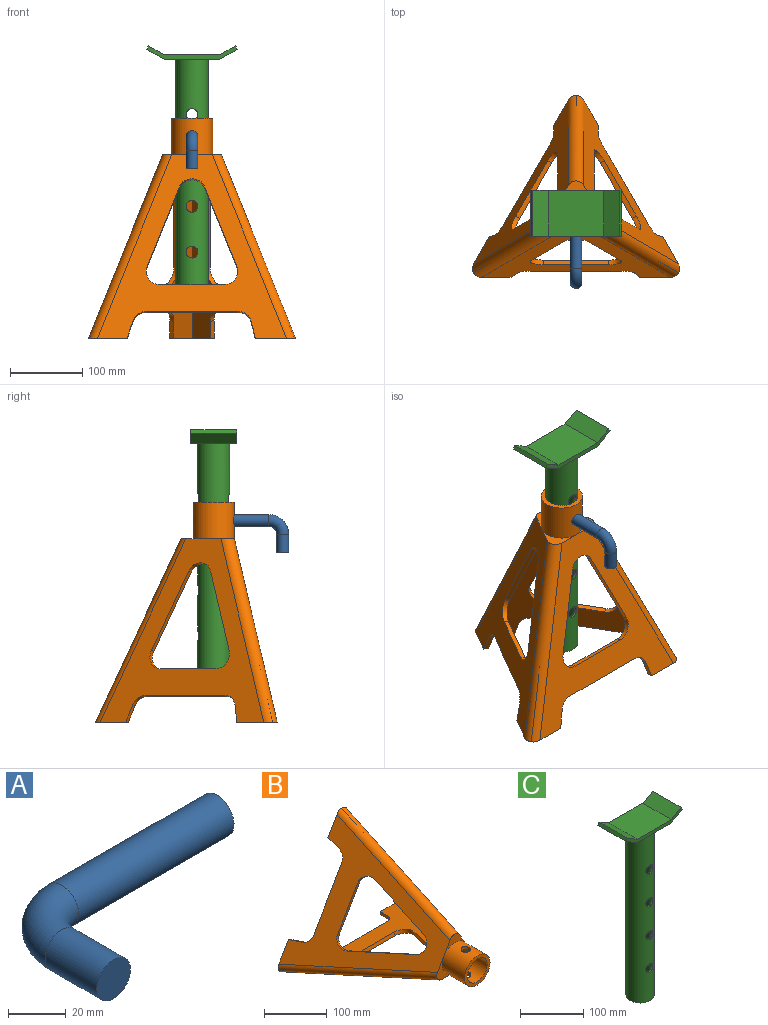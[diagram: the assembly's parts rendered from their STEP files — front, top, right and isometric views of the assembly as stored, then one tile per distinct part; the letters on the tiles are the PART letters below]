
ASSEMBLY  parts=3 mates=2
PART A: 5 faces, bbox 105.8x55x16.5 mm
  f0: plane 16.51x16.51mm, normal (0,-1,0), area 214.1mm2, adj f2
  f1: plane 16.51x16.51mm, normal (1,0,0), area 214.1mm2, adj f4
  f2: cylinder r=8.26mm len=25.4mm, axis (0,1,0), area 1317.4mm2, adj f0,f3
  f3: torus R=19.05mm, axis (0,0,-1), area 1552.1mm2, adj f2,f4
  f4: cylinder r=8.26mm len=76.2mm, axis (1,0,0), area 3952.3mm2, adj f1,f3
PART B: 56 faces, bbox 287.7x307.4x252.5 mm
  f0: plane 38.5x33.34mm, normal (0,1,0), area 338.3mm2, adj f4,f10,f15
  f1: plane 38.5x33.34mm, normal (0,1,0), area 338.3mm2, adj f7,f10,f15
  f2: plane 55.97x53.98mm, normal (0,1,0), area 638.6mm2, adj f3,f4,f6,f7,f20,f35,f45
  f3: plane 261.96x254mm, normal (0,-0.23,-0.97), area 22759.7mm2, adj f2,f8,f11,f13,f20,f21,f45,f46
  f4: plane 282.86x247.71mm, normal (0,0.23,0.97), area 27340.8mm2, adj f0,f2,f7,f8,f10,f14,f45,f46
  f5: plane 62.38x45.55mm, normal (0,1,0), area 624.7mm2, adj f6,f7,f9,f10,f22,f23,f34
  f6: plane 254x226.87mm, normal (-0.84,-0.23,0.49), area 22759.7mm2, adj f2,f5,f12,f13,f20,f22,f34,f35
  f7: plane 247.71x244.97mm, normal (0.84,0.23,-0.49), area 27340.8mm2, adj f1,f2,f4,f5,f10,f14,f34,f35
  f8: plane 56.09x55.97mm, normal (0,1,0), area 652.4mm2, adj f3,f4,f9,f10,f21,f27,f46
  f9: plane 254x226.87mm, normal (0.84,-0.23,0.49), area 22759.7mm2, adj f5,f8,f11,f12,f21,f22,f23,f24
  f10: plane 247.71x244.97mm, normal (-0.84,0.23,-0.49), area 27340.8mm2, adj f0,f1,f4,f5,f7,f8,f23,f24
  f11: plane 42.86x40.61mm, normal (0,-1,0), area 458.5mm2, adj f3,f9,f16,f21
  f12: plane 49.49x30.8mm, normal (0,-1,0), area 458.5mm2, adj f6,f9,f16,f22
  f13: plane 42.86x40.61mm, normal (0,-1,0), area 458.5mm2, adj f3,f6,f16,f20
  f14: plane 38.5x33.34mm, normal (0,1,0), area 338.3mm2, adj f4,f7,f15
  f15: cylinder r=22.23mm len=57.15mm, axis (0,1,0), area 7577.8mm2, adj f0,f1,f14,f17,f18,f19
  f16: cylinder r=28.57mm len=57.15mm, axis (0,1,0), area 8721mm2, adj f11,f12,f13,f17,f18,f19
  f17: plane 57.15x57.15mm, normal (0,-1,0), area 1013.4mm2, adj f15,f16
  f18: cylinder r=7.94mm len=15.88mm, axis (0,0,1), area 325mm2, adj f15,f16
  f19: cylinder r=7.94mm len=15.88mm, axis (0,0,1), area 325.1mm2, adj f15,f16
  f20: cylinder r=12.7mm len=258.99mm, axis (-0.37,0.91,-0.21), area 7146.4mm2, adj f2,f3,f6,f13
  f21: cylinder r=12.7mm len=258.99mm, axis (0.37,0.91,-0.21), area 7146.4mm2, adj f3,f8,f9,f11
  f22: cylinder r=12.7mm len=258.99mm, axis (0,0.91,0.42), area 7146.4mm2, adj f5,f6,f9,f12
  f23: plane 24.47x13.27mm, normal (0.54,0.31,-0.78), area 161mm2, adj f5,f9,f10,f24
  f24: cylinder r=19.05mm len=20.22mm, axis (0.84,-0.23,0.49), area 150.8mm2, adj f9,f10,f23,f25
  f25: plane 113.1x68.89mm, normal (0.2,0.97,0.11), area 811.7mm2, adj f9,f10,f24,f26
  f26: cylinder r=19.05mm len=17.51mm, axis (0.84,-0.23,0.49), area 161mm2, adj f9,f10,f25,f27
  f27: plane 22.96x12.86mm, normal (-0.44,0.23,0.87), area 146.9mm2, adj f8,f9,f10,f26
  f28: cylinder r=19.05mm len=34.33mm, axis (0.84,-0.23,0.49), area 338.7mm2, adj f9,f10,f29,f33
  f29: plane 111.25x50.69mm, normal (-0.39,0.36,0.85), area 857mm2, adj f9,f10,f28,f30
  f30: cylinder r=19.05mm len=26.9mm, axis (0.84,-0.23,0.49), area 247.8mm2, adj f9,f10,f29,f31
  f31: plane 80.21x50.02mm, normal (-0.2,-0.97,-0.11), area 587.4mm2, adj f9,f10,f30,f32
  f32: cylinder r=19.05mm len=26.9mm, axis (0.84,-0.23,0.49), area 247.8mm2, adj f9,f10,f31,f33
  f33: plane 111.25x54.93mm, normal (0.54,0.36,-0.76), area 857mm2, adj f9,f10,f28,f32
  f34: plane 24.47x13.27mm, normal (-0.54,0.31,-0.78), area 161mm2, adj f5,f6,f7,f38
  f35: plane 22.96x12.86mm, normal (0.44,0.23,0.87), area 146.9mm2, adj f2,f6,f7,f36
  f36: cylinder r=19.05mm len=17.51mm, axis (-0.84,-0.23,0.49), area 161mm2, adj f6,f7,f35,f37
  f37: plane 113.1x68.89mm, normal (-0.2,0.97,0.11), area 811.7mm2, adj f6,f7,f36,f38
  f38: cylinder r=19.05mm len=20.22mm, axis (-0.84,-0.23,0.49), area 150.8mm2, adj f6,f7,f34,f37
  f39: cylinder r=19.05mm len=34.33mm, axis (-0.84,-0.23,0.49), area 338.7mm2, adj f6,f7,f40,f44
  f40: plane 111.25x54.93mm, normal (-0.54,0.36,-0.76), area 857mm2, adj f6,f7,f39,f41
  f41: cylinder r=19.05mm len=26.9mm, axis (-0.84,-0.23,0.49), area 247.8mm2, adj f6,f7,f40,f42
  f42: plane 80.21x50.02mm, normal (0.2,-0.97,-0.11), area 587.4mm2, adj f6,f7,f41,f43
  f43: cylinder r=19.05mm len=26.9mm, axis (-0.84,-0.23,0.49), area 247.8mm2, adj f6,f7,f42,f44
  f44: plane 111.25x50.69mm, normal (0.39,0.36,0.85), area 857mm2, adj f6,f7,f39,f43
  f45: plane 24.47x11.88mm, normal (0.95,0.31,-0.07), area 161mm2, adj f2,f3,f4,f49
  f46: plane 22.96x11.51mm, normal (-0.97,0.23,-0.05), area 146.9mm2, adj f3,f4,f8,f47
  f47: cylinder r=19.05mm len=18.5mm, axis (0,-0.23,-0.97), area 161mm2, adj f3,f4,f46,f48
  f48: plane 127x6.22mm, normal (0,0.97,-0.23), area 811.7mm2, adj f3,f4,f47,f49
  f49: cylinder r=19.05mm len=18.05mm, axis (0,-0.23,-0.97), area 150.8mm2, adj f3,f4,f45,f48
  f50: cylinder r=19.05mm len=35.44mm, axis (0,-0.23,-0.97), area 338.7mm2, adj f3,f4,f51,f55
  f51: plane 111.25x44.45mm, normal (0.93,0.36,-0.08), area 857mm2, adj f3,f4,f50,f52
  f52: cylinder r=19.05mm len=26.9mm, axis (0,-0.23,-0.97), area 247.8mm2, adj f3,f4,f51,f53
  f53: plane 88.9x6.43mm, normal (0,-0.97,0.23), area 587.4mm2, adj f3,f4,f52,f54
  f54: cylinder r=19.05mm len=26.9mm, axis (0,-0.23,-0.97), area 247.8mm2, adj f3,f4,f53,f55
  f55: plane 111.25x44.45mm, normal (-0.93,0.36,-0.08), area 857mm2, adj f3,f4,f50,f54
PART C: 22 faces, bbox 125.7x63.5x349.3 mm
  f0: cylinder r=19.05mm len=330.2mm, axis (0,0,-1), area 37769.2mm2, adj f2,f7,f14,f15,f16,f17,f18,f19
  f1: cylinder r=22.23mm len=330.2mm, axis (0,0,-1), area 44369.6mm2, adj f2,f3,f14,f15,f16,f17,f18,f19
  f2: plane 44.45x44.45mm, normal (0,0,-1), area 411.7mm2, adj f0,f1
  f3: plane 76.2x63.5mm, normal (0,0,-1), area 3286.9mm2, adj f1,f5,f6,f9,f13
  f4: plane 76.2x63.5mm, normal (0,0,1), area 4838.7mm2, adj f5,f6,f8,f11
  f5: plane 125.69x19.05mm, normal (0,-1,0), area 780.7mm2, adj f3,f4,f8,f9,f10,f11,f12,f13
  f6: plane 125.69x19.05mm, normal (0,1,0), area 780.7mm2, adj f3,f4,f8,f9,f10,f11,f12,f13
  f7: plane 38.1x38.1mm, normal (0,0,-1), area 1140.1mm2, adj f0
  f8: plane 63.5x22mm, normal (-0.5,0,0.87), area 1612.9mm2, adj f4,f5,f6,f10
  f9: plane 63.5x24.75mm, normal (0.5,0,-0.87), area 1814.5mm2, adj f3,f5,f6,f10
  f10: plane 63.5x4.76mm, normal (0.87,0,0.5), area 349.2mm2, adj f5,f6,f8,f9
  f11: plane 63.5x22mm, normal (0.5,0,0.87), area 1612.9mm2, adj f4,f5,f6,f12
  f12: plane 63.5x4.76mm, normal (-0.87,0,0.5), area 349.2mm2, adj f5,f6,f11,f13
  f13: plane 63.5x24.75mm, normal (-0.5,0,-0.87), area 1814.5mm2, adj f3,f5,f6,f12
  f14: cylinder r=8.26mm len=16.51mm, axis (0,-1,0), area 172mm2, adj f0,f1
  f15: cylinder r=8.26mm len=16.51mm, axis (0,-1,0), area 172mm2, adj f0,f1
  f16: cylinder r=8.26mm len=16.51mm, axis (0,-1,0), area 172mm2, adj f0,f1
  f17: cylinder r=8.26mm len=16.51mm, axis (0,-1,0), area 172mm2, adj f0,f1
  f18: cylinder r=8.26mm len=16.51mm, axis (0,-1,0), area 172mm2, adj f0,f1
  f19: cylinder r=8.26mm len=16.51mm, axis (0,-1,0), area 172mm2, adj f0,f1
  f20: cylinder r=8.26mm len=16.51mm, axis (0,-1,0), area 172mm2, adj f0,f1
  f21: cylinder r=8.26mm len=16.51mm, axis (0,-1,0), area 172mm2, adj f0,f1
PLACE A rot(axis=(0.58,0.58,0.58),120deg) t=(361.9,-41.31,258.78)mm
PLACE B rot(axis=(-1,0,0),90deg) t=(361.9,193.3,23.83)mm
PLACE C t=(361.9,17.32,244.76)mm
MATE slider B.f15 <-> C.f1  axis (0,0,-1) through (361.9,17.32,300.06)mm
MATE slider A.f4 <-> B.f18  axis (0,1,0) through (361.9,-21.16,303.23)mm
